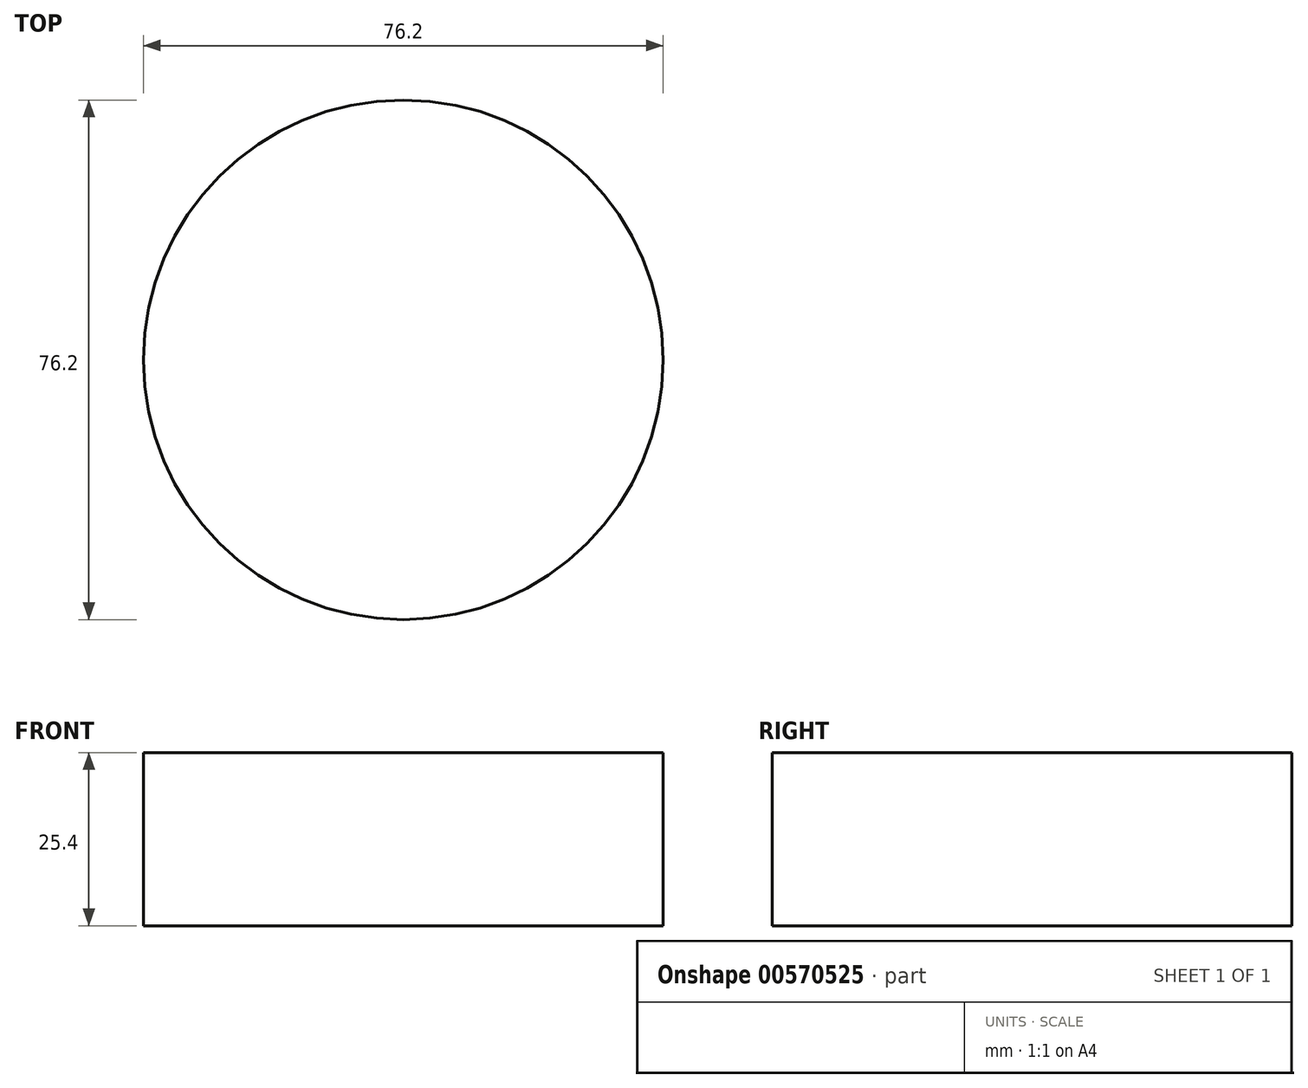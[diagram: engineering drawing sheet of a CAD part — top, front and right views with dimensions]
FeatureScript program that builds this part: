
annotation { "Feature Type Name" : "Feature", "Feature Type Description" : "" }
export const myFeature = defineFeature(function(context is Context, id is Id, definition is map)
    precondition{}
    {
        {
            var Q0;
            Q0=qCreatedBy(makeId("Top.planeOp"),FACE);
            var sketch = newSketch(context, id + "F0", { "sketchPlane" : qUnion([Q0])});
            skLineSegment(sketch, "E0", {"start": v(-50.19, -1.3) * mm, "end": v(0.61, -1.3) * mm});
            skLineSegment(sketch, "E1", {"start": v(-52.04, -24.47) * mm, "end": v(24.16, -24.47) * mm});
            skLineSegment(sketch, "E2", {"start": v(-53.9, -40.37) * mm, "end": v(47.7, -40.37) * mm});
            skCircle(sketch, "E3", {"center": v(0, 69.74) * mm, "radius": 38.1 * mm});
            skLineSegment(sketch, "E4", {"start": v(-55.28, -70) * mm, "end": v(97.12, -70) * mm});
            skSolve(sketch);
        }
        {
            var Q0;
            Q0=sQuery(id+"F0.wireOp",EDGE,"E3");
            extrude(context, id + "F1", {"bodyType" : ToolBodyType.SURFACE, "surfaceEntities" : qUnion([Q0]), "depth" : 25.4 * mm, "offsetDistance" : 25.4 * mm});
        }
    });
